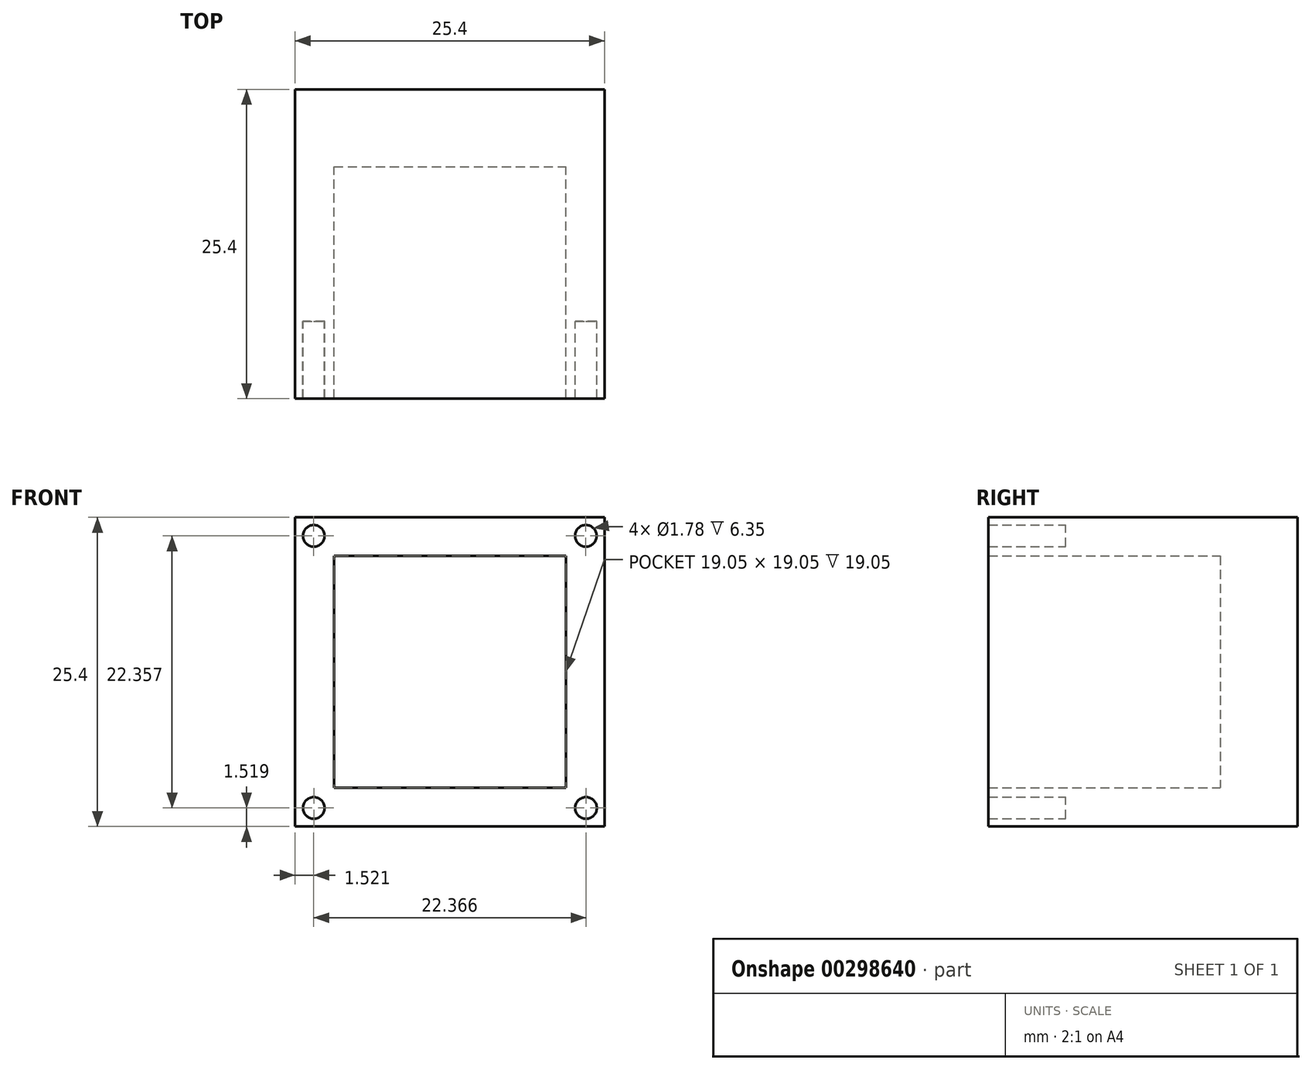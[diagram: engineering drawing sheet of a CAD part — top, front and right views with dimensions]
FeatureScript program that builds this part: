
annotation { "Feature Type Name" : "Feature", "Feature Type Description" : "" }
export const myFeature = defineFeature(function(context is Context, id is Id, definition is map)
    precondition{}
    {
        {
            var Q0;
            Q0=qCreatedBy(makeId("Front.planeOp"),FACE);
            var sketch = newSketch(context, id + "F0", { "sketchPlane" : qUnion([Q0])});
            skPoint(sketch, "E0.middle", {"position": v(0, 0) * mm});
            skLineSegment(sketch, "E1.bottom", {"start": v(12.7, 12.7) * mm, "end": v(-12.7, 12.7) * mm});
            skLineSegment(sketch, "E1.top", {"start": v(12.7, -12.7) * mm, "end": v(-12.7, -12.7) * mm});
            skLineSegment(sketch, "E1.left", {"start": v(12.7, 12.7) * mm, "end": v(12.7, -12.7) * mm});
            skLineSegment(sketch, "E1.right", {"start": v(-12.7, 12.7) * mm, "end": v(-12.7, -12.7) * mm});
            skLineSegment(sketch, "E2.bottom", {"start": v(9.53, 9.53) * mm, "end": v(-9.53, 9.53) * mm});
            skLineSegment(sketch, "E2.top", {"start": v(9.53, -9.53) * mm, "end": v(-9.53, -9.53) * mm});
            skLineSegment(sketch, "E2.left", {"start": v(9.53, 9.53) * mm, "end": v(9.53, -9.53) * mm});
            skLineSegment(sketch, "E2.right", {"start": v(-9.53, 9.53) * mm, "end": v(-9.53, -9.53) * mm});
            skCircle(sketch, "E3", {"center": v(-11.18, 11.17) * mm, "radius": 0.89 * mm});
            skCircle(sketch, "E4", {"center": v(-11.17, -11.18) * mm, "radius": 0.89 * mm});
            skCircle(sketch, "E5", {"center": v(11.19, -11.18) * mm, "radius": 0.89 * mm});
            skLineSegment(sketch, "E6", {"start": v(12.7, 12.7) * mm, "end": v(11.18, 12.7) * mm});
            skLineSegment(sketch, "E7", {"start": v(11.18, 12.7) * mm, "end": v(11.18, 11.18) * mm});
            skCircle(sketch, "E8", {"center": v(11.18, 11.18) * mm, "radius": 0.89 * mm});
            skLineSegment(sketch, "E9", {"start": v(12.7, -12.7) * mm, "end": v(11.18, -12.7) * mm});
            skLineSegment(sketch, "E10", {"start": v(11.18, -12.7) * mm, "end": v(11.18, -11.18) * mm});
            skLineSegment(sketch, "E11", {"start": v(-12.7, -12.7) * mm, "end": v(-11.18, -12.7) * mm});
            skLineSegment(sketch, "E12", {"start": v(-11.18, -12.7) * mm, "end": v(-11.18, -11.18) * mm});
            skLineSegment(sketch, "E13", {"start": v(-12.7, 12.7) * mm, "end": v(-11.18, 12.7) * mm});
            skLineSegment(sketch, "E14", {"start": v(-11.18, 12.7) * mm, "end": v(-11.18, 11.18) * mm});
            skSolve(sketch);
        }
        {
            var Q0;
            Q0 = qSketchRegion(id + "F0", true);
            extrude(context, id + "F1", {"entities" : qUnion([Q0]), "depth" : 25.4 * mm});
        }
        {
            var Q0;
            Q0=qCreatedBy(makeId("Front.planeOp"),FACE);
            var sketch = newSketch(context, id + "F2", { "sketchPlane" : qUnion([Q0])});
            skLineSegment(sketch, "E15.bottom", {"start": v(-9.52, 9.53) * mm, "end": v(9.53, 9.53) * mm});
            skLineSegment(sketch, "E15.top", {"start": v(-9.53, -9.53) * mm, "end": v(9.52, -9.53) * mm});
            skLineSegment(sketch, "E15.left", {"start": v(-9.52, 9.53) * mm, "end": v(-9.53, -9.53) * mm});
            skLineSegment(sketch, "E15.right", {"start": v(9.53, 9.53) * mm, "end": v(9.52, -9.53) * mm});
            skPoint(sketch, "E15.middle", {"position": v(0, 0) * mm});
            skSolve(sketch);
        }
        {
            var Q0;
            Q0=makeQuery(id+"F2.imprint","IMPRINT",FACE,{"disambiguationData":[TD([[makeQuery(id+"F2.imprint","IMPRINT",EDGE,{"derivedFrom":sQuery(id+"F2.wireOp",EDGE,"E15.bottom")}),-1.0]])]});
            extrude(context, id + "F3", {"entities" : qUnion([Q0]), "operationType" : NewBodyOperationType.ADD, "depth" : 6.35 * mm});
        }
        {
            var Q0;
            Q0=makeQuery(id+"F3.boolean.opBoolean","MERGE",FACE,{"derivedFrom":[makeQuery(id+"F1.opExtrude","CAP_FACE",FACE,{"disambiguationData":[OSD([sQuery(id+"F0.wireOp",EDGE,"E1.bottom"),sQuery(id+"F0.wireOp",EDGE,"E1.top"),sQuery(id+"F0.wireOp",EDGE,"E1.left"),sQuery(id+"F0.wireOp",EDGE,"E1.right"),sQuery(id+"F0.wireOp",EDGE,"E2.bottom"),sQuery(id+"F0.wireOp",EDGE,"E2.top"),sQuery(id+"F0.wireOp",EDGE,"E2.left"),sQuery(id+"F0.wireOp",EDGE,"E2.right"),sQuery(id+"F0.wireOp",EDGE,"E3"),sQuery(id+"F0.wireOp",EDGE,"E4"),sQuery(id+"F0.wireOp",EDGE,"E5"),sQuery(id+"F0.wireOp",EDGE,"E6"),sQuery(id+"F0.wireOp",EDGE,"E8"),sQuery(id+"F0.wireOp",EDGE,"E9"),sQuery(id+"F0.wireOp",EDGE,"E11"),sQuery(id+"F0.wireOp",EDGE,"E13")])],"isStart":true}),makeQuery(id+"F3.opExtrude","CAP_FACE",FACE,{"disambiguationData":[OSD([sQuery(id+"F2.wireOp",EDGE,"E15.bottom"),sQuery(id+"F2.wireOp",EDGE,"E15.top"),sQuery(id+"F2.wireOp",EDGE,"E15.left"),sQuery(id+"F2.wireOp",EDGE,"E15.right")])],"isStart":true})]});
            var sketch = newSketch(context, id + "F4", { "sketchPlane" : qUnion([Q0])});
            skCircle(sketch, "E16", {"center": v(11.18, 11.17) * mm, "radius": 0.89 * mm});
            skCircle(sketch, "E17", {"center": v(-11.19, -11.18) * mm, "radius": 0.89 * mm});
            skCircle(sketch, "E18", {"center": v(11.17, -11.18) * mm, "radius": 0.89 * mm});
            skCircle(sketch, "E19", {"center": v(-11.18, 11.18) * mm, "radius": 0.89 * mm});
            skSolve(sketch);
        }
        {
            var Q0;
            Q0 = qSketchRegion(id + "F4", true);
            extrude(context, id + "F5", {"entities" : qUnion([Q0]), "operationType" : NewBodyOperationType.ADD, "oppositeDirection" : true, "depth" : 19.05 * mm});
        }
    });
